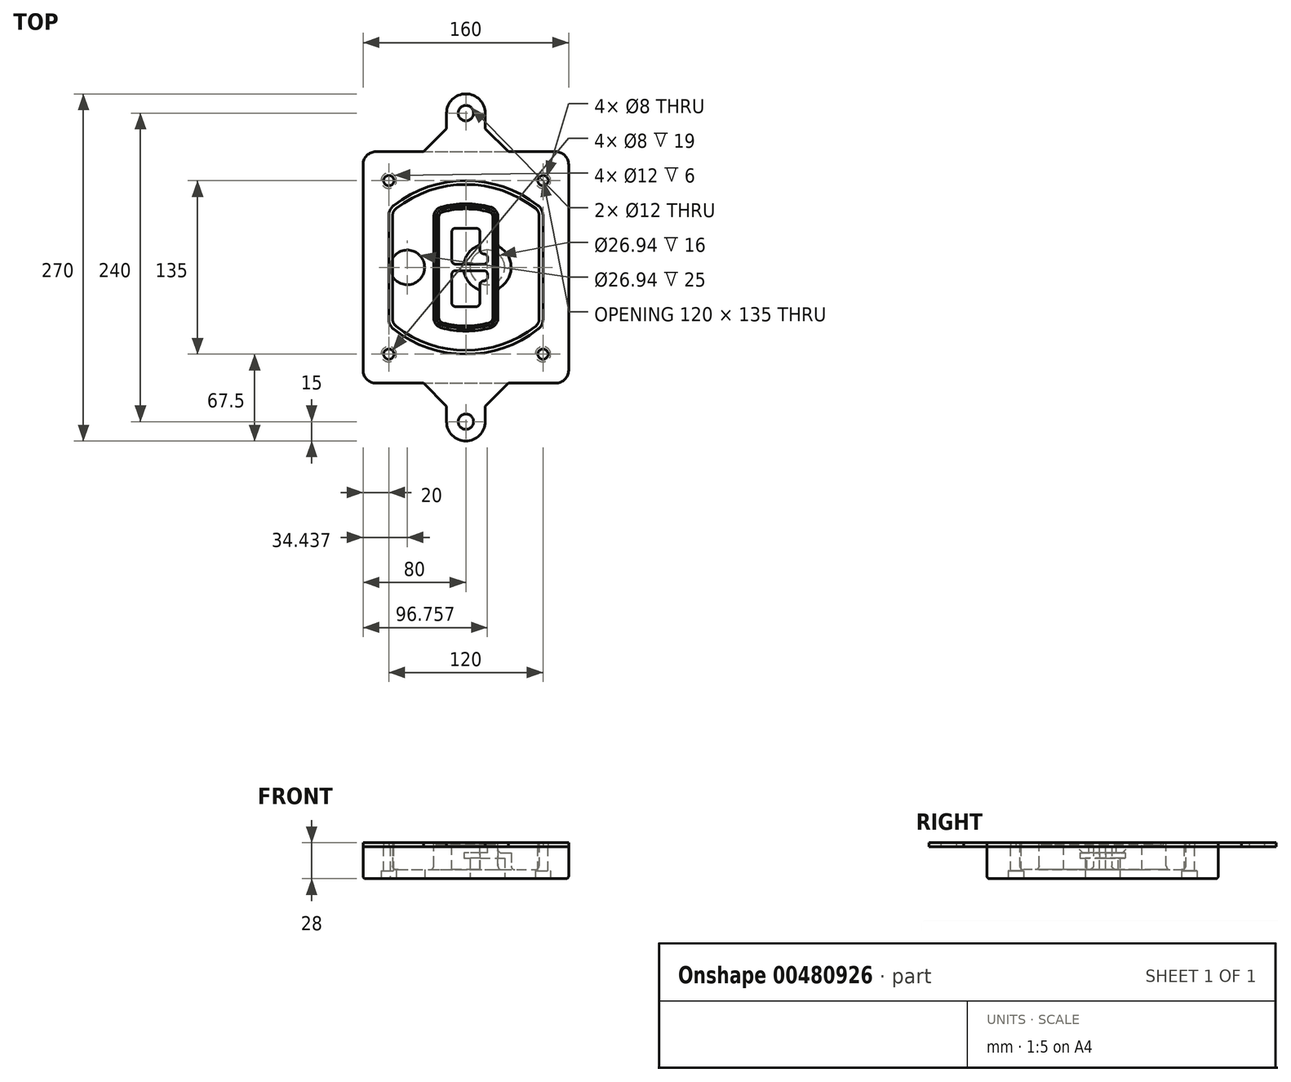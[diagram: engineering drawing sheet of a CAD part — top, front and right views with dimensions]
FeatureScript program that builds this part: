
annotation { "Feature Type Name" : "Feature", "Feature Type Description" : "" }
export const myFeature = defineFeature(function(context is Context, id is Id, definition is map)
    precondition{}
    {
        {
            var Q0;
            Q0=qCreatedBy(makeId("Top.planeOp"),FACE);
            var sketch = newSketch(context, id + "F0", { "sketchPlane" : qUnion([Q0])});
            skPoint(sketch, "E0.rect.middle", {"position": v(0, 0) * mm});
            skLineSegment(sketch, "E1.bottom", {"start": v(-70, -90) * mm, "end": v(70, -90) * mm});
            skLineSegment(sketch, "E1.top", {"start": v(-70, 90) * mm, "end": v(70, 90) * mm});
            skLineSegment(sketch, "E1.left", {"start": v(-80, -80) * mm, "end": v(-80, 80) * mm});
            skLineSegment(sketch, "E1.right", {"start": v(80, -80) * mm, "end": v(80, 80) * mm});
            skLineSegment(sketch, "E2", {"start": v(-80, 90) * mm, "end": v(80, -90) * mm, "construction": true});
            skLineSegment(sketch, "E3", {"start": v(80, 90) * mm, "end": v(-80, -90) * mm, "construction": true});
            skCircle(sketch, "E4", {"center": v(-60, 67.5) * mm, "radius": 4 * mm});
            skCircle(sketch, "E5", {"center": v(60, 67.5) * mm, "radius": 4 * mm});
            skCircle(sketch, "E6", {"center": v(60, -67.5) * mm, "radius": 4 * mm});
            skCircle(sketch, "E7", {"center": v(-60, -67.5) * mm, "radius": 4 * mm});
            skLineSegment(sketch, "E8", {"start": v(-60, 67.5) * mm, "end": v(60, 67.5) * mm, "construction": true});
            skLineSegment(sketch, "E9", {"start": v(60, 67.5) * mm, "end": v(60, -67.5) * mm, "construction": true});
            skLineSegment(sketch, "E10", {"start": v(60, -67.5) * mm, "end": v(-60, -67.5) * mm, "construction": true});
            skLineSegment(sketch, "E11", {"start": v(-60, -67.5) * mm, "end": v(-60, 67.5) * mm, "construction": true});
            skLineSegment(sketch, "E12", {"start": v(-60, 40.3) * mm, "end": v(-60, -40.3) * mm});
            skLineSegment(sketch, "E13", {"start": v(60, 40.3) * mm, "end": v(60, -40.3) * mm});
            skArc(sketch, "E14", {"start": v(56.15, 48.18) * mm, "mid": v(0, 67.5) * mm, "end": v(-56.15, 48.18) * mm});
            skArc(sketch, "E15", {"start": v(-56.15, -48.18) * mm, "mid": v(0, -67.5) * mm, "end": v(56.15, -48.18) * mm});
            skLineSegment(sketch, "E16", {"start": v(-60, 0) * mm, "end": v(60, 0) * mm, "construction": true});
            skPoint(sketch, "E17.visualSharp", {"position": v(-60, -45) * mm});
            skArc(sketch, "E17.filletArc", {"start": v(-60, -40.3) * mm, "mid": v(-58.99, -44.68) * mm, "end": v(-56.15, -48.18) * mm});
            skPoint(sketch, "E18.visualSharp", {"position": v(-60, 45) * mm});
            skArc(sketch, "E18.filletArc", {"start": v(-56.15, 48.18) * mm, "mid": v(-58.99, 44.68) * mm, "end": v(-60, 40.3) * mm});
            skPoint(sketch, "E19.visualSharp", {"position": v(60, 45) * mm});
            skArc(sketch, "E19.filletArc", {"start": v(60, 40.3) * mm, "mid": v(58.99, 44.68) * mm, "end": v(56.15, 48.18) * mm});
            skPoint(sketch, "E20.visualSharp", {"position": v(60, -45) * mm});
            skArc(sketch, "E20.filletArc", {"start": v(56.15, -48.18) * mm, "mid": v(58.99, -44.68) * mm, "end": v(60, -40.3) * mm});
            skPoint(sketch, "E21.visualSharp", {"position": v(-80, 90) * mm});
            skArc(sketch, "E21.filletArc", {"start": v(-70, 90) * mm, "mid": v(-77.07, 87.07) * mm, "end": v(-80, 80) * mm});
            skPoint(sketch, "E22.visualSharp", {"position": v(80, 90) * mm});
            skArc(sketch, "E22.filletArc", {"start": v(80, 80) * mm, "mid": v(77.07, 87.07) * mm, "end": v(70, 90) * mm});
            skPoint(sketch, "E23.visualSharp", {"position": v(80, -90) * mm});
            skArc(sketch, "E23.filletArc", {"start": v(70, -90) * mm, "mid": v(77.07, -87.07) * mm, "end": v(80, -80) * mm});
            skPoint(sketch, "E24.visualSharp", {"position": v(-80, -90) * mm});
            skArc(sketch, "E24.filletArc", {"start": v(-80, -80) * mm, "mid": v(-77.07, -87.07) * mm, "end": v(-70, -90) * mm});
            skArc(sketch, "E25.0", {"start": v(57, 40.3) * mm, "mid": v(56.3, 43.36) * mm, "end": v(54.3, 45.81) * mm});
            skLineSegment(sketch, "E25.1", {"start": v(57, 40.3) * mm, "end": v(57, -40.3) * mm});
            skArc(sketch, "E25.2", {"start": v(54.3, -45.81) * mm, "mid": v(56.3, -43.36) * mm, "end": v(57, -40.3) * mm});
            skArc(sketch, "E25.3", {"start": v(-54.3, -45.81) * mm, "mid": v(0, -64.5) * mm, "end": v(54.3, -45.81) * mm});
            skArc(sketch, "E25.4", {"start": v(-57, -40.3) * mm, "mid": v(-56.3, -43.36) * mm, "end": v(-54.3, -45.81) * mm});
            skArc(sketch, "E25.5", {"start": v(54.3, 45.81) * mm, "mid": v(0, 64.5) * mm, "end": v(-54.3, 45.81) * mm});
            skLineSegment(sketch, "E25.6", {"start": v(-57, 40.3) * mm, "end": v(-57, -40.3) * mm});
            skArc(sketch, "E25.7", {"start": v(-54.3, 45.81) * mm, "mid": v(-56.3, 43.36) * mm, "end": v(-57, 40.3) * mm});
            skArc(sketch, "E26.0", {"start": v(-58.62, 51.33) * mm, "mid": v(-62.58, 46.43) * mm, "end": v(-64, 40.3) * mm});
            skArc(sketch, "E26.1", {"start": v(58.62, 51.33) * mm, "mid": v(0, 71.5) * mm, "end": v(-58.62, 51.33) * mm});
            skArc(sketch, "E26.2", {"start": v(64, 40.3) * mm, "mid": v(62.58, 46.43) * mm, "end": v(58.62, 51.33) * mm});
            skLineSegment(sketch, "E26.3", {"start": v(64, 40.3) * mm, "end": v(64, -40.3) * mm});
            skArc(sketch, "E26.4", {"start": v(58.62, -51.33) * mm, "mid": v(62.58, -46.43) * mm, "end": v(64, -40.3) * mm});
            skLineSegment(sketch, "E26.5", {"start": v(-64, 40.3) * mm, "end": v(-64, -40.3) * mm});
            skArc(sketch, "E26.6", {"start": v(-58.62, -51.33) * mm, "mid": v(0, -71.5) * mm, "end": v(58.62, -51.33) * mm});
            skArc(sketch, "E26.7", {"start": v(-64, -40.3) * mm, "mid": v(-62.58, -46.43) * mm, "end": v(-58.62, -51.33) * mm});
            skSolve(sketch);
        }
        {
            var Q0;
            Q0=makeQuery(id+"F0.imprint","IMPRINT",FACE,{"disambiguationData":[TD([[makeQuery(id+"F0.imprint","IMPRINT",EDGE,{"derivedFrom":sQuery(id+"F0.wireOp",EDGE,"E1.bottom")}),1.0]])]});
            var Q1;
            Q1=makeQuery(id+"F0.imprint","IMPRINT",FACE,{"disambiguationData":[TD([[makeQuery(id+"F0.imprint","IMPRINT",EDGE,{"derivedFrom":sQuery(id+"F0.wireOp",EDGE,"E12")}),1.0]])]});
            var Q2;
            Q2=makeQuery(id+"F0.imprint","IMPRINT",FACE,{"disambiguationData":[TD([[makeQuery(id+"F0.imprint","IMPRINT",EDGE,{"derivedFrom":sQuery(id+"F0.wireOp",EDGE,"E25.0")}),1.0]])]});
            var Q3;
            Q3=makeQuery(id+"F0.imprint","IMPRINT",FACE,{"disambiguationData":[TD([[makeQuery(id+"F0.imprint","IMPRINT",EDGE,{"derivedFrom":sQuery(id+"F0.wireOp",EDGE,"E12")}),-1.0]])]});
            extrude(context, id + "F1", {"entities" : qUnion([Q0, Q1, Q2, Q3]), "oppositeDirection" : true, "depth" : 25 * mm});
        }
        {
            var Q0;
            Q0=makeQuery(id+"F0.imprint","IMPRINT",FACE,{"disambiguationData":[TD([[makeQuery(id+"F0.imprint","IMPRINT",EDGE,{"derivedFrom":sQuery(id+"F0.wireOp",EDGE,"E12")}),1.0]])]});
            extrude(context, id + "F2", {"entities" : qUnion([Q0]), "operationType" : NewBodyOperationType.ADD, "depth" : 3 * mm});
        }
        {
            var Q0;
            Q0=makeQuery(id+"F0.imprint","IMPRINT",FACE,{"disambiguationData":[TD([[makeQuery(id+"F0.imprint","IMPRINT",EDGE,{"derivedFrom":sQuery(id+"F0.wireOp",EDGE,"E25.0")}),1.0]])]});
            extrude(context, id + "F3", {"entities" : qUnion([Q0]), "operationType" : NewBodyOperationType.REMOVE, "oppositeDirection" : true, "depth" : 18 * mm});
        }
        {
            var Q0;
            Q0=makeQuery(id+"F2.opExtrude","CAP_FACE",FACE,{"disambiguationData":[OSD([sQuery(id+"F0.wireOp",EDGE,"E12"),sQuery(id+"F0.wireOp",EDGE,"E13"),sQuery(id+"F0.wireOp",EDGE,"E14"),sQuery(id+"F0.wireOp",EDGE,"E15"),sQuery(id+"F0.wireOp",EDGE,"E17.filletArc"),sQuery(id+"F0.wireOp",EDGE,"E18.filletArc"),sQuery(id+"F0.wireOp",EDGE,"E19.filletArc"),sQuery(id+"F0.wireOp",EDGE,"E20.filletArc"),sQuery(id+"F0.wireOp",EDGE,"E25.0"),sQuery(id+"F0.wireOp",EDGE,"E25.1"),sQuery(id+"F0.wireOp",EDGE,"E25.2"),sQuery(id+"F0.wireOp",EDGE,"E25.3"),sQuery(id+"F0.wireOp",EDGE,"E25.4"),sQuery(id+"F0.wireOp",EDGE,"E25.5"),sQuery(id+"F0.wireOp",EDGE,"E25.6"),sQuery(id+"F0.wireOp",EDGE,"E25.7")])],"isStart":false});
            var sketch = newSketch(context, id + "F4", { "sketchPlane" : qUnion([Q0])});
            skArc(sketch, "E27.0", {"start": v(-19.08, -46.97) * mm, "mid": v(0, -49.5) * mm, "end": v(19.08, -46.97) * mm});
            skArc(sketch, "E28.0", {"start": v(19.08, 46.97) * mm, "mid": v(0, 49.5) * mm, "end": v(-19.08, 46.97) * mm});
            skLineSegment(sketch, "E29", {"start": v(-25, 39.25) * mm, "end": v(-25, -39.25) * mm});
            skLineSegment(sketch, "E30", {"start": v(25, 39.25) * mm, "end": v(25, -39.25) * mm});
            skLineSegment(sketch, "E31", {"start": v(-25, 45.1) * mm, "end": v(25, 45.1) * mm, "construction": true});
            skLineSegment(sketch, "E32", {"start": v(-25, -45.1) * mm, "end": v(25, -45.1) * mm, "construction": true});
            skPoint(sketch, "E33.visualSharp", {"position": v(-25, 45.1) * mm});
            skArc(sketch, "E33.filletArc", {"start": v(-19.08, 46.97) * mm, "mid": v(-23.35, 44.11) * mm, "end": v(-25, 39.25) * mm});
            skPoint(sketch, "E34.visualSharp", {"position": v(25, 45.1) * mm});
            skArc(sketch, "E34.filletArc", {"start": v(25, 39.25) * mm, "mid": v(23.35, 44.11) * mm, "end": v(19.08, 46.97) * mm});
            skPoint(sketch, "E35.visualSharp", {"position": v(25, -45.1) * mm});
            skArc(sketch, "E35.filletArc", {"start": v(19.08, -46.97) * mm, "mid": v(23.35, -44.11) * mm, "end": v(25, -39.25) * mm});
            skPoint(sketch, "E36.visualSharp", {"position": v(-25, -45.1) * mm});
            skArc(sketch, "E36.filletArc", {"start": v(-25, -39.25) * mm, "mid": v(-23.35, -44.11) * mm, "end": v(-19.08, -46.97) * mm});
            skArc(sketch, "E37.0", {"start": v(54.3, 45.81) * mm, "mid": v(0, 64.5) * mm, "end": v(-54.3, 45.81) * mm});
            skArc(sketch, "E37.1", {"start": v(-54.3, 45.81) * mm, "mid": v(-56.3, 43.36) * mm, "end": v(-57, 40.3) * mm});
            skLineSegment(sketch, "E37.2", {"start": v(-57, 40.3) * mm, "end": v(-57, -40.3) * mm});
            skArc(sketch, "E37.3", {"start": v(-57, -40.3) * mm, "mid": v(-56.3, -43.36) * mm, "end": v(-54.3, -45.81) * mm});
            skArc(sketch, "E37.4", {"start": v(-54.3, -45.81) * mm, "mid": v(0, -64.5) * mm, "end": v(54.3, -45.81) * mm});
            skArc(sketch, "E37.5", {"start": v(54.3, -45.81) * mm, "mid": v(56.3, -43.36) * mm, "end": v(57, -40.3) * mm});
            skLineSegment(sketch, "E37.6", {"start": v(57, 40.3) * mm, "end": v(57, -40.3) * mm});
            skArc(sketch, "E37.7", {"start": v(57, 40.3) * mm, "mid": v(56.3, 43.36) * mm, "end": v(54.3, 45.81) * mm});
            skLineSegment(sketch, "E38.0", {"start": v(23, 39.25) * mm, "end": v(23, -39.25) * mm});
            skArc(sketch, "E38.1", {"start": v(18.56, -45.04) * mm, "mid": v(21.76, -42.9) * mm, "end": v(23, -39.25) * mm});
            skArc(sketch, "E38.2", {"start": v(-18.56, -45.04) * mm, "mid": v(0, -47.5) * mm, "end": v(18.56, -45.04) * mm});
            skArc(sketch, "E38.3", {"start": v(-23, -39.25) * mm, "mid": v(-21.76, -42.9) * mm, "end": v(-18.56, -45.04) * mm});
            skLineSegment(sketch, "E38.4", {"start": v(-23, 39.25) * mm, "end": v(-23, -39.25) * mm});
            skArc(sketch, "E38.5", {"start": v(23, 39.25) * mm, "mid": v(21.76, 42.9) * mm, "end": v(18.56, 45.04) * mm});
            skArc(sketch, "E38.6", {"start": v(-18.56, 45.04) * mm, "mid": v(-21.76, 42.9) * mm, "end": v(-23, 39.25) * mm});
            skArc(sketch, "E38.7", {"start": v(18.56, 45.04) * mm, "mid": v(0, 47.5) * mm, "end": v(-18.56, 45.04) * mm});
            skArc(sketch, "E39.0", {"start": v(21, 39.25) * mm, "mid": v(20.18, 41.68) * mm, "end": v(18.04, 43.1) * mm});
            skLineSegment(sketch, "E39.1", {"start": v(21, 39.25) * mm, "end": v(21, -39.25) * mm});
            skArc(sketch, "E39.2", {"start": v(18.04, -43.1) * mm, "mid": v(20.18, -41.68) * mm, "end": v(21, -39.25) * mm});
            skArc(sketch, "E39.3", {"start": v(-18.04, -43.1) * mm, "mid": v(0, -45.5) * mm, "end": v(18.04, -43.1) * mm});
            skArc(sketch, "E39.4", {"start": v(-21, -39.25) * mm, "mid": v(-20.18, -41.68) * mm, "end": v(-18.04, -43.1) * mm});
            skArc(sketch, "E39.5", {"start": v(18.04, 43.1) * mm, "mid": v(0, 45.5) * mm, "end": v(-18.04, 43.1) * mm});
            skLineSegment(sketch, "E39.6", {"start": v(-21, 39.25) * mm, "end": v(-21, -39.25) * mm});
            skArc(sketch, "E39.7", {"start": v(-18.04, 43.1) * mm, "mid": v(-20.18, 41.68) * mm, "end": v(-21, 39.25) * mm});
            skLineSegment(sketch, "E40", {"start": v(-25, 0) * mm, "end": v(25, 0) * mm, "construction": true});
            skLineSegment(sketch, "E41", {"start": v(-11, 5.5) * mm, "end": v(-11, 27.5) * mm});
            skLineSegment(sketch, "E42", {"start": v(-8, 30.5) * mm, "end": v(8, 30.5) * mm});
            skLineSegment(sketch, "E43", {"start": v(11, 27.5) * mm, "end": v(11, 13.5) * mm});
            skLineSegment(sketch, "E44", {"start": v(14, 10.5) * mm, "end": v(14, 10.5) * mm});
            skLineSegment(sketch, "E45", {"start": v(17, 7.5) * mm, "end": v(17, 5.5) * mm});
            skLineSegment(sketch, "E46", {"start": v(14, 2.5) * mm, "end": v(-8, 2.5) * mm});
            skPoint(sketch, "E47.visualSharp", {"position": v(-11, 30.5) * mm});
            skArc(sketch, "E47.filletArc", {"start": v(-8, 30.5) * mm, "mid": v(-10.12, 29.62) * mm, "end": v(-11, 27.5) * mm});
            skPoint(sketch, "E48.visualSharp", {"position": v(11, 30.5) * mm});
            skArc(sketch, "E48.filletArc", {"start": v(11, 27.5) * mm, "mid": v(10.12, 29.62) * mm, "end": v(8, 30.5) * mm});
            skPoint(sketch, "E49.visualSharp", {"position": v(11, 10.5) * mm});
            skArc(sketch, "E49.filletArc", {"start": v(11, 13.5) * mm, "mid": v(11.88, 11.38) * mm, "end": v(14, 10.5) * mm});
            skPoint(sketch, "E50.visualSharp", {"position": v(17, 10.5) * mm});
            skArc(sketch, "E50.filletArc", {"start": v(17, 7.5) * mm, "mid": v(16.12, 9.62) * mm, "end": v(14, 10.5) * mm});
            skPoint(sketch, "E51.visualSharp", {"position": v(17, 2.5) * mm});
            skArc(sketch, "E51.filletArc", {"start": v(14, 2.5) * mm, "mid": v(16.12, 3.38) * mm, "end": v(17, 5.5) * mm});
            skPoint(sketch, "E52.visualSharp", {"position": v(-11, 2.5) * mm});
            skArc(sketch, "E52.filletArc", {"start": v(-11, 5.5) * mm, "mid": v(-10.12, 3.38) * mm, "end": v(-8, 2.5) * mm});
            skLineSegment(sketch, "E53.0.MirrorCS", {"start": v(14, -2.5) * mm, "end": v(-8, -2.5) * mm});
            skArc(sketch, "E54.0.MirrorCS", {"start": v(-11, -5.5) * mm, "mid": v(-10.12, -3.38) * mm, "end": v(-8, -2.5) * mm});
            skLineSegment(sketch, "E55.0.MirrorCS", {"start": v(-11, -5.5) * mm, "end": v(-11, -27.5) * mm});
            skArc(sketch, "E56.0.MirrorCS", {"start": v(-8, -30.5) * mm, "mid": v(-10.12, -29.62) * mm, "end": v(-11, -27.5) * mm});
            skLineSegment(sketch, "E57.0.MirrorCS", {"start": v(-8, -30.5) * mm, "end": v(8, -30.5) * mm});
            skArc(sketch, "E58.0.MirrorCS", {"start": v(11, -27.5) * mm, "mid": v(10.12, -29.62) * mm, "end": v(8, -30.5) * mm});
            skLineSegment(sketch, "E59.0.MirrorCS", {"start": v(11, -27.5) * mm, "end": v(11, -13.5) * mm});
            skArc(sketch, "E60.0.MirrorCS", {"start": v(11, -13.5) * mm, "mid": v(11.88, -11.38) * mm, "end": v(14, -10.5) * mm});
            skArc(sketch, "E61.0.MirrorCS", {"start": v(17, -7.5) * mm, "mid": v(16.12, -9.62) * mm, "end": v(14, -10.5) * mm});
            skLineSegment(sketch, "E62.0.MirrorCS", {"start": v(17, -7.5) * mm, "end": v(17, -5.5) * mm});
            skArc(sketch, "E63.0.MirrorCS", {"start": v(14, -2.5) * mm, "mid": v(16.12, -3.38) * mm, "end": v(17, -5.5) * mm});
            skSolve(sketch);
        }
        {
            var Q0;
            Q0=makeQuery(id+"F4.imprint","IMPRINT",FACE,{"disambiguationData":[TD([[makeQuery(id+"F4.imprint","IMPRINT",EDGE,{"derivedFrom":sQuery(id+"F4.wireOp",EDGE,"E27.0")}),1.0]])]});
            var Q1;
            Q1=makeQuery(id+"F4.imprint","IMPRINT",FACE,{"disambiguationData":[TD([[makeQuery(id+"F4.imprint","IMPRINT",EDGE,{"derivedFrom":sQuery(id+"F4.wireOp",EDGE,"E38.0")}),-1.0]])]});
            var Q2;
            Q2=makeQuery(id+"F4.imprint","IMPRINT",FACE,{"disambiguationData":[TD([[makeQuery(id+"F4.imprint","IMPRINT",EDGE,{"derivedFrom":sQuery(id+"F4.wireOp",EDGE,"E39.0")}),1.0]])]});
            extrude(context, id + "F5", {"entities" : qUnion([Q0, Q1, Q2]), "operationType" : NewBodyOperationType.ADD, "endBound" : BoundingType.UP_TO_NEXT, "oppositeDirection" : true, "depth" : 25 * mm});
        }
        {
            var Q0;
            Q0=makeQuery(id+"F4.imprint","IMPRINT",FACE,{"disambiguationData":[TD([[makeQuery(id+"F4.imprint","IMPRINT",EDGE,{"derivedFrom":sQuery(id+"F4.wireOp",EDGE,"E38.0")}),-1.0]])]});
            extrude(context, id + "F6", {"entities" : qUnion([Q0]), "operationType" : NewBodyOperationType.REMOVE, "oppositeDirection" : true, "depth" : 2 * mm});
        }
        {
            var Q0;
            Q0=makeQuery(id+"F1.opExtrude","CAP_FACE",FACE,{"disambiguationData":[OSD([sQuery(id+"F0.wireOp",EDGE,"E1.bottom"),sQuery(id+"F0.wireOp",EDGE,"E1.top"),sQuery(id+"F0.wireOp",EDGE,"E1.left"),sQuery(id+"F0.wireOp",EDGE,"E1.right"),sQuery(id+"F0.wireOp",EDGE,"E4"),sQuery(id+"F0.wireOp",EDGE,"E5"),sQuery(id+"F0.wireOp",EDGE,"E6"),sQuery(id+"F0.wireOp",EDGE,"E7"),sQuery(id+"F0.wireOp",EDGE,"E21.filletArc"),sQuery(id+"F0.wireOp",EDGE,"E22.filletArc"),sQuery(id+"F0.wireOp",EDGE,"E23.filletArc"),sQuery(id+"F0.wireOp",EDGE,"E24.filletArc")])],"isStart":false});
            var sketch = newSketch(context, id + "F7", { "sketchPlane" : qUnion([Q0])});
            skCircle(sketch, "E64", {"center": v(16.76, 0) * mm, "radius": 13.47 * mm});
            skCircle(sketch, "E65", {"center": v(-45.56, 0) * mm, "radius": 13.47 * mm});
            skLineSegment(sketch, "E66", {"start": v(80, 0) * mm, "end": v(-80, 0) * mm});
            skCircle(sketch, "E67", {"center": v(16.76, 0) * mm, "radius": 18.47 * mm});
            skCircle(sketch, "E68", {"center": v(60, -67.5) * mm, "radius": 6 * mm});
            skCircle(sketch, "E69", {"center": v(-60, -67.5) * mm, "radius": 6 * mm});
            skCircle(sketch, "E70", {"center": v(-60, 67.5) * mm, "radius": 6 * mm});
            skCircle(sketch, "E71", {"center": v(60, 67.5) * mm, "radius": 6 * mm});
            skSolve(sketch);
        }
        {
            var Q0;
            {var subQ1=sQuery(id+"F7.wireOp",EDGE,"E66");var subQ4=sQuery(id+"F7.wireOp",EDGE,"E64");var subQ6=makeQuery(id+"F7.imprint","INTERSECT",VERTEX,{"disambiguationData":[OD(0.0)],"derivedFrom":[subQ4,subQ1]});Q0=makeQuery(id+"F7.imprint","IMPRINT",FACE,{"disambiguationData":[TD([[makeQuery(id+"F7.imprint","IMPRINT",EDGE,{"disambiguationData":[TD([[subQ6,-1.0]])],"derivedFrom":subQ4}),-1.0]])]});}
            var Q1;
            {var subQ0=sQuery(id+"F7.wireOp",EDGE,"E66");var subQ1=sQuery(id+"F7.wireOp",EDGE,"E64");var subQ3=makeQuery(id+"F7.imprint","INTERSECT",VERTEX,{"disambiguationData":[OD(0.0)],"derivedFrom":[subQ1,subQ0]});Q1=makeQuery(id+"F7.imprint","IMPRINT",FACE,{"disambiguationData":[TD([[makeQuery(id+"F7.imprint","IMPRINT",EDGE,{"disambiguationData":[TD([[subQ3,-1.0]])],"derivedFrom":subQ1}),1.0]])]});}
            var Q2;
            {var subQ0=sQuery(id+"F7.wireOp",EDGE,"E66");var subQ1=sQuery(id+"F7.wireOp",EDGE,"E64");var subQ3=makeQuery(id+"F7.imprint","INTERSECT",VERTEX,{"disambiguationData":[OD(0.0)],"derivedFrom":[subQ1,subQ0]});Q2=makeQuery(id+"F7.imprint","IMPRINT",FACE,{"disambiguationData":[TD([[makeQuery(id+"F7.imprint","IMPRINT",EDGE,{"disambiguationData":[TD([[subQ3,1.0]])],"derivedFrom":subQ1}),1.0]])]});}
            var Q3;
            {var subQ1=sQuery(id+"F7.wireOp",EDGE,"E66");var subQ4=sQuery(id+"F7.wireOp",EDGE,"E64");var subQ6=makeQuery(id+"F7.imprint","INTERSECT",VERTEX,{"disambiguationData":[OD(0.0)],"derivedFrom":[subQ4,subQ1]});Q3=makeQuery(id+"F7.imprint","IMPRINT",FACE,{"disambiguationData":[TD([[makeQuery(id+"F7.imprint","IMPRINT",EDGE,{"disambiguationData":[TD([[subQ6,1.0]])],"derivedFrom":subQ4}),-1.0]])]});}
            extrude(context, id + "F8", {"entities" : qUnion([Q0, Q1, Q2, Q3]), "operationType" : NewBodyOperationType.ADD, "oppositeDirection" : true, "depth" : 20 * mm});
        }
        {
            var Q0;
            {var subQ0=sQuery(id+"F7.wireOp",EDGE,"E66");var subQ1=sQuery(id+"F7.wireOp",EDGE,"E64");var subQ3=makeQuery(id+"F7.imprint","INTERSECT",VERTEX,{"disambiguationData":[OD(0.0)],"derivedFrom":[subQ1,subQ0]});Q0=makeQuery(id+"F7.imprint","IMPRINT",FACE,{"disambiguationData":[TD([[makeQuery(id+"F7.imprint","IMPRINT",EDGE,{"disambiguationData":[TD([[subQ3,-1.0]])],"derivedFrom":subQ1}),1.0]])]});}
            var Q1;
            {var subQ0=sQuery(id+"F7.wireOp",EDGE,"E66");var subQ1=sQuery(id+"F7.wireOp",EDGE,"E64");var subQ3=makeQuery(id+"F7.imprint","INTERSECT",VERTEX,{"disambiguationData":[OD(0.0)],"derivedFrom":[subQ1,subQ0]});Q1=makeQuery(id+"F7.imprint","IMPRINT",FACE,{"disambiguationData":[TD([[makeQuery(id+"F7.imprint","IMPRINT",EDGE,{"disambiguationData":[TD([[subQ3,1.0]])],"derivedFrom":subQ1}),1.0]])]});}
            extrude(context, id + "F9", {"entities" : qUnion([Q0, Q1]), "operationType" : NewBodyOperationType.REMOVE, "oppositeDirection" : true, "depth" : 16 * mm});
        }
        {
            var Q0;
            {var subQ0=sQuery(id+"F7.wireOp",EDGE,"E66");var subQ1=sQuery(id+"F7.wireOp",EDGE,"E65");var subQ3=makeQuery(id+"F7.imprint","INTERSECT",VERTEX,{"disambiguationData":[OD(0.0)],"derivedFrom":[subQ1,subQ0]});Q0=makeQuery(id+"F7.imprint","IMPRINT",FACE,{"disambiguationData":[TD([[makeQuery(id+"F7.imprint","IMPRINT",EDGE,{"disambiguationData":[TD([[subQ3,-1.0]])],"derivedFrom":subQ1}),1.0]])]});}
            var Q1;
            {var subQ0=sQuery(id+"F7.wireOp",EDGE,"E66");var subQ1=sQuery(id+"F7.wireOp",EDGE,"E65");var subQ3=makeQuery(id+"F7.imprint","INTERSECT",VERTEX,{"disambiguationData":[OD(0.0)],"derivedFrom":[subQ1,subQ0]});Q1=makeQuery(id+"F7.imprint","IMPRINT",FACE,{"disambiguationData":[TD([[makeQuery(id+"F7.imprint","IMPRINT",EDGE,{"disambiguationData":[TD([[subQ3,1.0]])],"derivedFrom":subQ1}),1.0]])]});}
            extrude(context, id + "F10", {"entities" : qUnion([Q0, Q1]), "operationType" : NewBodyOperationType.REMOVE, "oppositeDirection" : true, "depth" : 25 * mm});
        }
        {
            var Q0;
            Q0=makeQuery(id+"F7.imprint","IMPRINT",FACE,{"disambiguationData":[TD([[makeQuery(id+"F7.imprint","IMPRINT",EDGE,{"derivedFrom":sQuery(id+"F7.wireOp",EDGE,"E68")}),1.0]])]});
            var Q1;
            Q1=makeQuery(id+"F7.imprint","IMPRINT",FACE,{"disambiguationData":[TD([[makeQuery(id+"F7.imprint","IMPRINT",EDGE,{"derivedFrom":makeQuery(id+"F1.opExtrude","CAP_EDGE",EDGE,{"disambiguationData":[OSD([sQuery(id+"F0.wireOp",EDGE,"E5")])],"isStart":false})}),-1.0]])]});
            var Q2;
            Q2=makeQuery(id+"F7.imprint","IMPRINT",FACE,{"disambiguationData":[TD([[makeQuery(id+"F7.imprint","IMPRINT",EDGE,{"derivedFrom":sQuery(id+"F7.wireOp",EDGE,"E69")}),1.0]])]});
            var Q3;
            Q3=makeQuery(id+"F7.imprint","IMPRINT",FACE,{"disambiguationData":[TD([[makeQuery(id+"F7.imprint","IMPRINT",EDGE,{"derivedFrom":makeQuery(id+"F1.opExtrude","CAP_EDGE",EDGE,{"disambiguationData":[OSD([sQuery(id+"F0.wireOp",EDGE,"E4")])],"isStart":false})}),-1.0]])]});
            var Q4;
            Q4=makeQuery(id+"F7.imprint","IMPRINT",FACE,{"disambiguationData":[TD([[makeQuery(id+"F7.imprint","IMPRINT",EDGE,{"derivedFrom":sQuery(id+"F7.wireOp",EDGE,"E70")}),1.0]])]});
            var Q5;
            Q5=makeQuery(id+"F7.imprint","IMPRINT",FACE,{"disambiguationData":[TD([[makeQuery(id+"F7.imprint","IMPRINT",EDGE,{"derivedFrom":makeQuery(id+"F1.opExtrude","CAP_EDGE",EDGE,{"disambiguationData":[OSD([sQuery(id+"F0.wireOp",EDGE,"E7")])],"isStart":false})}),-1.0]])]});
            var Q6;
            Q6=makeQuery(id+"F7.imprint","IMPRINT",FACE,{"disambiguationData":[TD([[makeQuery(id+"F7.imprint","IMPRINT",EDGE,{"derivedFrom":sQuery(id+"F7.wireOp",EDGE,"E71")}),1.0]])]});
            var Q7;
            Q7=makeQuery(id+"F7.imprint","IMPRINT",FACE,{"disambiguationData":[TD([[makeQuery(id+"F7.imprint","IMPRINT",EDGE,{"derivedFrom":makeQuery(id+"F1.opExtrude","CAP_EDGE",EDGE,{"disambiguationData":[OSD([sQuery(id+"F0.wireOp",EDGE,"E6")])],"isStart":false})}),-1.0]])]});
            extrude(context, id + "F11", {"entities" : qUnion([Q0, Q1, Q2, Q3, Q4, Q5, Q6, Q7]), "operationType" : NewBodyOperationType.REMOVE, "oppositeDirection" : true, "depth" : 6 * mm});
        }
        {
            var Q0;
            Q0=makeQuery(id+"F9.boolean.opBoolean","COPY",FACE,{"derivedFrom":makeQuery(id+"F9.opExtrude","CAP_FACE",FACE,{"disambiguationData":[OSD([sQuery(id+"F7.wireOp",EDGE,"E64")])],"isStart":false})});
            var sketch = newSketch(context, id + "F12", { "sketchPlane" : qUnion([Q0])});
            skArc(sketch, "E72.0", {"start": v(11, 17.55) * mm, "mid": v(2.57, 11.82) * mm, "end": v(-1.54, 2.5) * mm});
            skArc(sketch, "E72.1", {"start": v(-1.54, -2.5) * mm, "mid": v(2.57, -11.82) * mm, "end": v(11, -17.55) * mm});
            skLineSegment(sketch, "E73", {"start": v(-1.54, -2.5) * mm, "end": v(14, -2.5) * mm});
            skLineSegment(sketch, "E74.0", {"start": v(14, 2.5) * mm, "end": v(-1.54, 2.5) * mm});
            skArc(sketch, "E74.1", {"start": v(14, 2.5) * mm, "mid": v(16.12, 3.38) * mm, "end": v(17, 5.5) * mm});
            skLineSegment(sketch, "E74.2", {"start": v(17, 7.5) * mm, "end": v(17, 5.5) * mm});
            skArc(sketch, "E74.3", {"start": v(17, 7.5) * mm, "mid": v(16.12, 9.62) * mm, "end": v(14, 10.5) * mm});
            skArc(sketch, "E74.4", {"start": v(11, 13.5) * mm, "mid": v(11.88, 11.38) * mm, "end": v(14, 10.5) * mm});
            skLineSegment(sketch, "E74.5", {"start": v(11, 17.55) * mm, "end": v(11, 13.5) * mm});
            skLineSegment(sketch, "E74.7", {"start": v(14, -2.5) * mm, "end": v(-1.54, -2.5) * mm});
            skArc(sketch, "E74.8", {"start": v(14, -2.5) * mm, "mid": v(16.12, -3.38) * mm, "end": v(17, -5.5) * mm});
            skLineSegment(sketch, "E74.9", {"start": v(17, -7.5) * mm, "end": v(17, -5.5) * mm});
            skArc(sketch, "E74.10", {"start": v(17, -7.5) * mm, "mid": v(16.12, -9.62) * mm, "end": v(14, -10.5) * mm});
            skArc(sketch, "E74.11", {"start": v(11, -13.5) * mm, "mid": v(11.88, -11.38) * mm, "end": v(14, -10.5) * mm});
            skLineSegment(sketch, "E74.12", {"start": v(11, -17.55) * mm, "end": v(11, -13.5) * mm});
            skPoint(sketch, "E75.orphan", {"position": v(11, -27.5) * mm});
            skPoint(sketch, "E76.orphan", {"position": v(-8, -2.5) * mm});
            skPoint(sketch, "E77.orphan", {"position": v(-8, 2.5) * mm});
            skPoint(sketch, "E78.orphan", {"position": v(11, 27.5) * mm});
            skSolve(sketch);
        }
        {
            var Q0;
            {var subQ7=sQuery(id+"F12.wireOp",EDGE,"E72.0");var subQ14=sQuery(id+"F12.wireOp",EDGE,"E72.1");var subQ16=sQuery(id+"F12.wireOp",EDGE,"E74.1");var subQ18=sQuery(id+"F12.wireOp",EDGE,"E74.8");Q0=qUnion([makeQuery(id+"F12.imprint","IMPRINT",FACE,{"disambiguationData":[TD([[makeQuery(id+"F12.imprint","IMPRINT",EDGE,{"derivedFrom":subQ7}),1.0]])]}),makeQuery(id+"F12.imprint","IMPRINT",FACE,{"disambiguationData":[TD([[makeQuery(id+"F12.imprint","IMPRINT",EDGE,{"derivedFrom":subQ14}),1.0]])]}),makeQuery(id+"F12.imprint","IMPRINT",FACE,{"disambiguationData":[TD([[makeQuery(id+"F12.imprint","IMPRINT",EDGE,{"derivedFrom":subQ16}),1.0]])]}),makeQuery(id+"F12.imprint","IMPRINT",FACE,{"disambiguationData":[TD([[makeQuery(id+"F12.imprint","IMPRINT",EDGE,{"derivedFrom":subQ18}),-1.0]])]})]);}
            var Q1;
            Q1=makeQuery(id+"F5.boolean.opBoolean","SPLIT",FACE,{"disambiguationData":[TD([makeQuery(id+"F5.opExtrude","SWEPT_FACE",FACE,{"disambiguationData":[OSD([sQuery(id+"F4.wireOp",EDGE,"E41")])]})])],"derivedFrom":makeQuery(id+"F3.boolean.opBoolean","COPY",FACE,{"derivedFrom":makeQuery(id+"F3.opExtrude","CAP_FACE",FACE,{"disambiguationData":[OSD([sQuery(id+"F0.wireOp",EDGE,"E25.0"),sQuery(id+"F0.wireOp",EDGE,"E25.1"),sQuery(id+"F0.wireOp",EDGE,"E25.2"),sQuery(id+"F0.wireOp",EDGE,"E25.3"),sQuery(id+"F0.wireOp",EDGE,"E25.4"),sQuery(id+"F0.wireOp",EDGE,"E25.5"),sQuery(id+"F0.wireOp",EDGE,"E25.6"),sQuery(id+"F0.wireOp",EDGE,"E25.7")])],"isStart":false})})});
            extrude(context, id + "F13", {"entities" : qUnion([Q0]), "operationType" : NewBodyOperationType.REMOVE, "endBound" : BoundingType.UP_TO_SURFACE, "endBoundEntityFace" : qUnion([Q1]), "depth" : 25 * mm});
        }
        {
            var Q0;
            Q0=makeQuery(id+"F3.boolean.opBoolean","COPY",EDGE,{"derivedFrom":makeQuery(id+"F3.opExtrude","CAP_EDGE",EDGE,{"disambiguationData":[OSD([sQuery(id+"F0.wireOp",EDGE,"E25.6")])],"isStart":false})});
            var Q1;
            Q1=makeQuery(id+"F8.boolean.opBoolean","INTERSECT",EDGE,{"derivedFrom":[makeQuery(id+"F5.opExtrude","SWEPT_FACE",FACE,{"disambiguationData":[OSD([sQuery(id+"F4.wireOp",EDGE,"E30")])]}),makeQuery(id+"F8.opExtrude","CAP_FACE",FACE,{"disambiguationData":[OSD([sQuery(id+"F7.wireOp",EDGE,"E67")])],"isStart":false})]});
            var Q2;
            Q2=makeQuery(id+"F8.boolean.opBoolean","INTERSECT",EDGE,{"disambiguationData":[OD(1.0)],"derivedFrom":[makeQuery(id+"F5.opExtrude","SWEPT_FACE",FACE,{"disambiguationData":[OSD([sQuery(id+"F4.wireOp",EDGE,"E30")])]}),makeQuery(id+"F8.opExtrude","SWEPT_FACE",FACE,{"disambiguationData":[OSD([sQuery(id+"F7.wireOp",EDGE,"E67")])]})]});
            var Q3;
            {var subQ0=sQuery(id+"F4.wireOp",EDGE,"E30");Q3=makeQuery(id+"F8.boolean.opBoolean","SPLIT",EDGE,{"disambiguationData":[TD([makeQuery(id+"F5.opExtrude","SWEPT_FACE",FACE,{"disambiguationData":[OSD([sQuery(id+"F4.wireOp",EDGE,"E35.filletArc")])]})])],"derivedFrom":makeQuery(id+"F5.opExtrude","CAP_EDGE",EDGE,{"disambiguationData":[OSD([subQ0])],"isStart":false})});}
            var Q4;
            {var subQ0=sQuery(id+"F0.wireOp",EDGE,"E25.7");var subQ1=sQuery(id+"F0.wireOp",EDGE,"E25.1");var subQ2=sQuery(id+"F0.wireOp",EDGE,"E25.6");var subQ3=sQuery(id+"F0.wireOp",EDGE,"E25.5");var subQ4=sQuery(id+"F0.wireOp",EDGE,"E25.4");var subQ5=sQuery(id+"F0.wireOp",EDGE,"E25.0");var subQ6=sQuery(id+"F0.wireOp",EDGE,"E25.2");var subQ7=sQuery(id+"F0.wireOp",EDGE,"E25.3");Q4=makeQuery(id+"F8.boolean.opBoolean","INTERSECT",EDGE,{"derivedFrom":[makeQuery(id+"F5.boolean.opBoolean","SPLIT",FACE,{"disambiguationData":[TD([makeQuery(id+"F2.opExtrude","SWEPT_FACE",FACE,{"disambiguationData":[OSD([subQ5])]})])],"derivedFrom":makeQuery(id+"F3.boolean.opBoolean","COPY",FACE,{"derivedFrom":makeQuery(id+"F3.opExtrude","CAP_FACE",FACE,{"disambiguationData":[OSD([subQ5,subQ1,subQ6,subQ7,subQ4,subQ3,subQ2,subQ0])],"isStart":false})})}),makeQuery(id+"F8.opExtrude","SWEPT_FACE",FACE,{"disambiguationData":[OSD([sQuery(id+"F7.wireOp",EDGE,"E67")])]})]});}
            var Q5;
            Q5=makeQuery(id+"F8.boolean.opBoolean","INTERSECT",EDGE,{"disambiguationData":[OD(0.0)],"derivedFrom":[makeQuery(id+"F5.opExtrude","SWEPT_FACE",FACE,{"disambiguationData":[OSD([sQuery(id+"F4.wireOp",EDGE,"E30")])]}),makeQuery(id+"F8.opExtrude","SWEPT_FACE",FACE,{"disambiguationData":[OSD([sQuery(id+"F7.wireOp",EDGE,"E67")])]})]});
            fillet(context, id + "F14", {"entities" : qUnion([Q0, Q1, Q2, Q3, Q4, Q5]), "radius" : 3 * mm, "tangentPropagation" : true, "allowEdgeOverflow" : false});
        }
        {
            var Q0;
            Q0=makeQuery(id+"F1.opExtrude","CAP_EDGE",EDGE,{"disambiguationData":[OSD([sQuery(id+"F0.wireOp",EDGE,"E1.bottom")])],"isStart":false});
            fillet(context, id + "F15", {"entities" : qUnion([Q0]), "radius" : 2 * mm, "tangentPropagation" : true, "allowEdgeOverflow" : false});
        }
        {
            var Q0;
            {var subQ0=sQuery(id+"F0.wireOp",EDGE,"E21.filletArc");var subQ1=sQuery(id+"F0.wireOp",EDGE,"E7");var subQ2=sQuery(id+"F0.wireOp",EDGE,"E6");var subQ3=sQuery(id+"F0.wireOp",EDGE,"E5");var subQ4=sQuery(id+"F0.wireOp",EDGE,"E4");var subQ5=sQuery(id+"F0.wireOp",EDGE,"E22.filletArc");var subQ6=sQuery(id+"F0.wireOp",EDGE,"E1.bottom");var subQ7=sQuery(id+"F0.wireOp",EDGE,"E1.right");var subQ8=sQuery(id+"F0.wireOp",EDGE,"E1.top");var subQ9=sQuery(id+"F0.wireOp",EDGE,"E1.left");var subQ10=sQuery(id+"F0.wireOp",EDGE,"E23.filletArc");var subQ11=sQuery(id+"F0.wireOp",EDGE,"E24.filletArc");Q0=makeQuery(id+"F2.boolean.opBoolean","SPLIT",FACE,{"disambiguationData":[TD([makeQuery(id+"F1.opExtrude","SWEPT_FACE",FACE,{"disambiguationData":[OSD([subQ6])]})])],"derivedFrom":makeQuery(id+"F1.opExtrude","CAP_FACE",FACE,{"disambiguationData":[OSD([subQ6,subQ8,subQ9,subQ7,subQ4,subQ3,subQ2,subQ1,subQ0,subQ5,subQ10,subQ11])],"isStart":true})});}
            var sketch = newSketch(context, id + "F16", { "sketchPlane" : qUnion([Q0])});
            skLineSegment(sketch, "E79", {"start": v(0, 90) * mm, "end": v(0, 120) * mm, "construction": true});
            skCircle(sketch, "E80", {"center": v(0, 120) * mm, "radius": 6 * mm});
            skLineSegment(sketch, "E81", {"start": v(-33, 90) * mm, "end": v(-15, 108) * mm});
            skLineSegment(sketch, "E82", {"start": v(-15, 108) * mm, "end": v(-15, 120) * mm});
            skLineSegment(sketch, "E83", {"start": v(33, 90) * mm, "end": v(15, 108) * mm});
            skLineSegment(sketch, "E84", {"start": v(15, 108) * mm, "end": v(15, 120) * mm});
            skArc(sketch, "E85", {"start": v(15, 120) * mm, "mid": v(0, 135) * mm, "end": v(-15, 120) * mm});
            skLineSegment(sketch, "E86", {"start": v(-80, 0) * mm, "end": v(80, 0) * mm, "construction": true});
            skLineSegment(sketch, "E87.MirrorCS", {"start": v(-15, -108) * mm, "end": v(-15, -120) * mm});
            skLineSegment(sketch, "E88.MirrorCS", {"start": v(15, -108) * mm, "end": v(15, -120) * mm});
            skLineSegment(sketch, "E89.MirrorCS", {"start": v(0, -90) * mm, "end": v(0, -120) * mm, "construction": true});
            skCircle(sketch, "E90.MirrorC", {"center": v(0, -120) * mm, "radius": 6 * mm});
            skLineSegment(sketch, "E91.MirrorCS", {"start": v(-33, -90) * mm, "end": v(-15, -108) * mm});
            skLineSegment(sketch, "E92.MirrorCS", {"start": v(33, -90) * mm, "end": v(15, -108) * mm});
            skArc(sketch, "E93.MirrorCS", {"start": v(15, -120) * mm, "mid": v(0, -135) * mm, "end": v(-15, -120) * mm});
            skSolve(sketch);
        }
        {
            var Q0;
            Q0=makeQuery(id+"F16.imprint","IMPRINT",FACE,{"disambiguationData":[TD([[makeQuery(id+"F16.imprint","IMPRINT",EDGE,{"derivedFrom":sQuery(id+"F16.wireOp",EDGE,"E87.MirrorCS")}),1.0]])]});
            var Q1;
            Q1=makeQuery(id+"F16.imprint","IMPRINT",FACE,{"disambiguationData":[TD([[makeQuery(id+"F16.imprint","IMPRINT",EDGE,{"derivedFrom":sQuery(id+"F16.wireOp",EDGE,"E80")}),-1.0]])]});
            var Q2;
            Q2=makeQuery(id+"F16.imprint","IMPRINT",FACE,{"disambiguationData":[TD([[makeQuery(id+"F16.imprint","IMPRINT",EDGE,{"derivedFrom":makeQuery(id+"F1.opExtrude","CAP_EDGE",EDGE,{"disambiguationData":[OSD([sQuery(id+"F0.wireOp",EDGE,"E1.left")])],"isStart":true})}),-1.0]])]});
            var Q3;
            Q3=makeQuery(id+"F2.opExtrude","CAP_FACE",FACE,{"disambiguationData":[OSD([sQuery(id+"F0.wireOp",EDGE,"E12"),sQuery(id+"F0.wireOp",EDGE,"E13"),sQuery(id+"F0.wireOp",EDGE,"E14"),sQuery(id+"F0.wireOp",EDGE,"E15"),sQuery(id+"F0.wireOp",EDGE,"E17.filletArc"),sQuery(id+"F0.wireOp",EDGE,"E18.filletArc"),sQuery(id+"F0.wireOp",EDGE,"E19.filletArc"),sQuery(id+"F0.wireOp",EDGE,"E20.filletArc"),sQuery(id+"F0.wireOp",EDGE,"E25.0"),sQuery(id+"F0.wireOp",EDGE,"E25.1"),sQuery(id+"F0.wireOp",EDGE,"E25.2"),sQuery(id+"F0.wireOp",EDGE,"E25.3"),sQuery(id+"F0.wireOp",EDGE,"E25.4"),sQuery(id+"F0.wireOp",EDGE,"E25.5"),sQuery(id+"F0.wireOp",EDGE,"E25.6"),sQuery(id+"F0.wireOp",EDGE,"E25.7")])],"isStart":false});
            extrude(context, id + "F17", {"entities" : qUnion([Q0, Q1, Q2]), "endBound" : BoundingType.UP_TO_SURFACE, "endBoundEntityFace" : qUnion([Q3]), "depth" : 25 * mm});
        }
    });
